FREECAD ASSEMBLY — COMPONENT RECIPES ("Pince_noisette")

This assembly document has 3 components, labeled P0..P2 below (a component is one placed body or linked part). 1 of them carries a construction recipe — the FreeCAD feature program that regenerates the part from scratch, quoted from this document or its linked companion documents; the rest are supplied as boundary geometry only. No exploded tour is included for this assembly.
COMPONENT P0 — recipe-attached ("Caisse de noisette001", modeled in this document).
Construction recipe (the document's own serialized feature program — sketch geometry with constraints, then the solid features built on it; lengths are millimeters unless a unit is written):

FEATURE [Sketcher::SketchObject] Sketch227
  ArcFitTolerance = 1e-06
  AttachmentSupport = -> [XY_Plane289]
  ExternalTypes = [0]
  FullyConstrained = true
  MakeInternals = false
  MapMode = 5
  _ExternalGeoVersion = 0
  sketch-geometry (4):
    g0: LineSegment StartX=-75 StartY=25 StartZ=0 EndX=-75 EndY=-25 EndZ=0
    g1: LineSegment StartX=-75 StartY=-25 StartZ=0 EndX=75 EndY=-25 EndZ=0
    g2: LineSegment StartX=75 StartY=-25 StartZ=0 EndX=75 EndY=25 EndZ=0
    g3: LineSegment StartX=75 StartY=25 StartZ=0 EndX=-75 EndY=25 EndZ=0
  constraints (11):
    c: Coincident(g0,g1)
    c: Coincident(g1,g2)
    c: Coincident(g2,g3)
    c: Coincident(g3,g0)
    c: Vertical(g0)
    c: Vertical(g2)
    c: Horizontal(g1)
    c: Horizontal(g3)
    c: Symmetric(g0,g1,g-1)
    c: DistanceX(g3,g3) = 150
    c: DistanceY(g2,g2) = 50
FEATURE [PartDesign::Pad] Pad114
  Direction = (0,0,1)
  Length = 30
  Length2 = 10
  Profile = -> Sketch227
  ReferenceAxis = -> Sketch227 [N_Axis]
  SideType = 0
  Suppressed = false
  Type = 0
  Type2 = 0
FEATURE [PartDesign::Body] Body093  label="Caisse de noisette"
  AllowCompound = false
  Group = -> [Sketch227,Pad114]
  Origin = -> Origin292
  Placement = pos=(55,0,-35) rot=(0,0,1;0rad)
  Tip = -> Pad114
COMPONENT P1 — geometry summary ("Pince_noisette"; no construction recipe available for this part):
  bounding box: 286.0 x 236.0 x 160.1 mm
  tessellated surface: 77,426 triangles
  volume: 107369 mm^3 (1% of its bounding box)
  symmetry: mirror-symmetric across its y mid-plane
COMPONENT P2 — geometry summary ("Robot_CRLG_base"; no construction recipe available for this part):
  bounding box: 342.0 x 320.0 x 207.6 mm
  tessellated surface: 174,788 triangles
  volume: 1317422 mm^3 (6% of its bounding box)
  symmetry: mirror-symmetric across its y mid-plane
PROVENANCE & LICENSES
A FreeCAD (.FCStd) document from a public repository crawl; recipes are the document's own serialized feature recipes (and, for linked parts, companion documents' recipes).
License: as declared in the source repository (recorded in the dataset sidecar).
